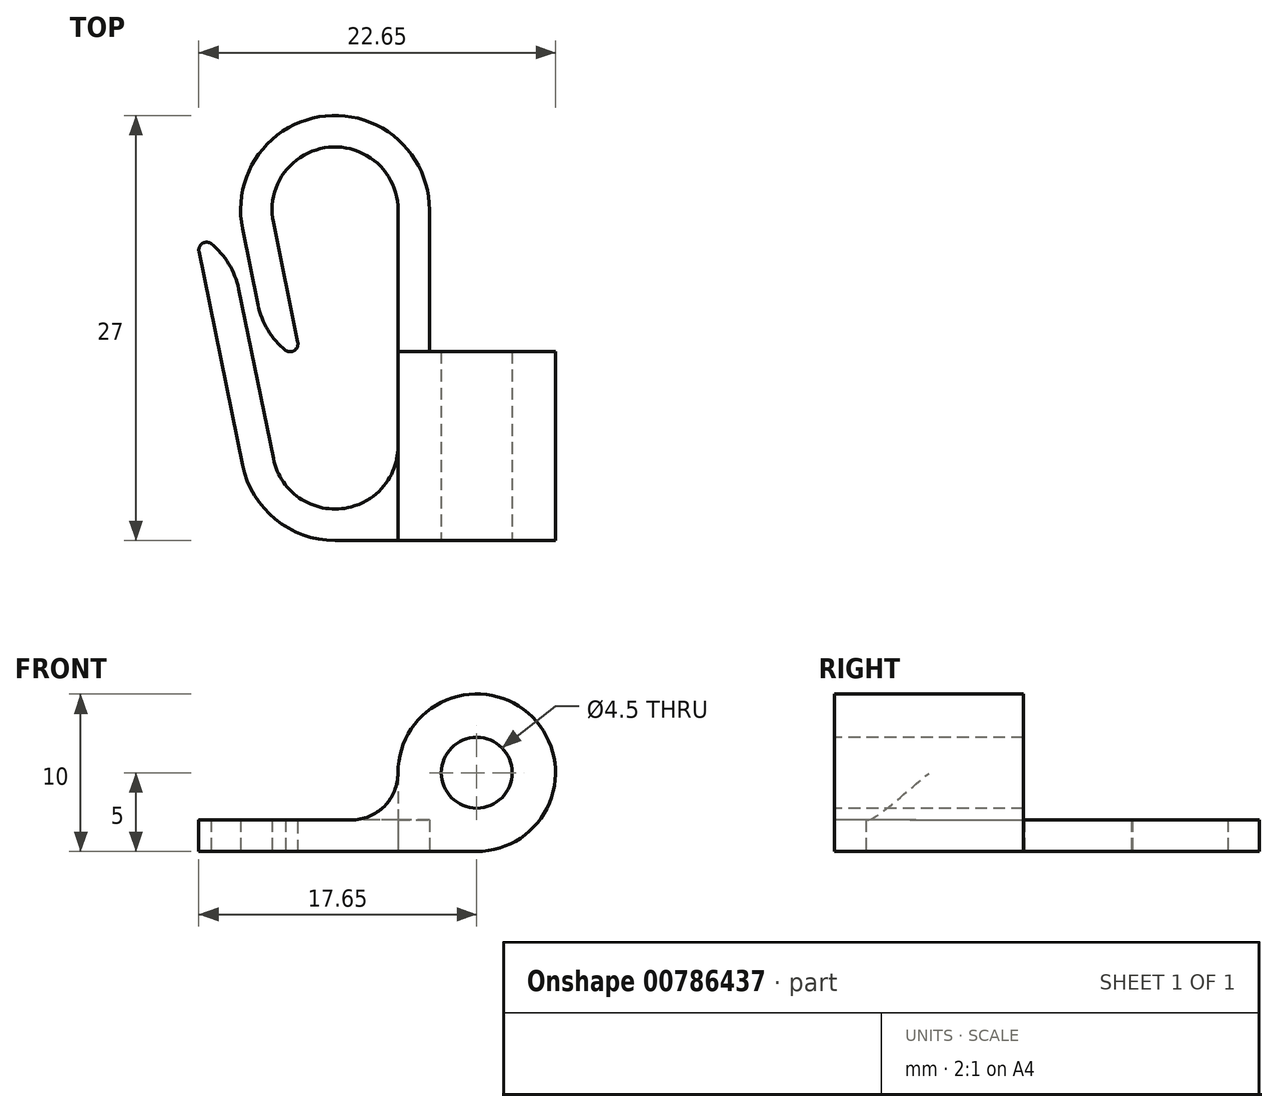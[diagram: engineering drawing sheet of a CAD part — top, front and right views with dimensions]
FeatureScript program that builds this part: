
annotation { "Feature Type Name" : "Feature", "Feature Type Description" : "" }
export const myFeature = defineFeature(function(context is Context, id is Id, definition is map)
    precondition{}
    {
        {
            var Q0;
            Q0=qCreatedBy(makeId("Top.planeOp"),FACE);
            var sketch = newSketch(context, id + "F0", { "sketchPlane" : qUnion([Q0])});
            skCircle(sketch, "E0", {"center": v(0, -5) * mm, "radius": 2.25 * mm});
            skCircle(sketch, "E1", {"center": v(0, -5) * mm, "radius": 5 * mm});
            skSolve(sketch);
        }
        {
            var Q0;
            Q0 = qSketchRegion(id + "F0", true);
            extrude(context, id + "F1", {"entities" : qUnion([Q0]), "endBound" : BoundingType.SYMMETRIC, "depth" : 12 * mm, "offsetDistance" : 25 * mm});
        }
        {
            var Q0;
            Q0=qCreatedBy(makeId("Front.planeOp"),FACE);
            var sketch = newSketch(context, id + "F2", { "sketchPlane" : qUnion([Q0])});
            skLineSegment(sketch, "E2", {"start": v(0, 23.91) * mm, "end": v(0, -9.96) * mm, "construction": true});
            skArc(sketch, "E3", {"start": v(-3, 15) * mm, "mid": v(-9.6, 20.97) * mm, "end": v(-14.88, 13.8) * mm});
            skArc(sketch, "E4", {"start": v(-5, 15) * mm, "mid": v(-9.4, 18.98) * mm, "end": v(-12.92, 14.2) * mm});
            skArc(sketch, "E5", {"start": v(-14.88, -1.2) * mm, "mid": v(-12.8, -4.65) * mm, "end": v(-9, -6) * mm});
            skArc(sketch, "E6", {"start": v(-12.92, -0.8) * mm, "mid": v(-8.6, -3.98) * mm, "end": v(-5, 0) * mm});
            skLineSegment(sketch, "E7", {"start": v(-3, 15) * mm, "end": v(-3, 6) * mm});
            skLineSegment(sketch, "E8", {"start": v(-5, 15) * mm, "end": v(-5, 0) * mm});
            skLineSegment(sketch, "E9", {"start": v(-14.88, -1.2) * mm, "end": v(-17.89, 13.53) * mm});
            skLineSegment(sketch, "E10", {"start": v(-12.92, -0.8) * mm, "end": v(-15.53, 11.97) * mm});
            skLineSegment(sketch, "E11", {"start": v(-14.88, 13.8) * mm, "end": v(-13.48, 6.97) * mm});
            skLineSegment(sketch, "E12", {"start": v(-12.92, 14.2) * mm, "end": v(-11.13, 5.41) * mm});
            skLineSegment(sketch, "E13", {"start": v(-13.48, 6.97) * mm, "end": v(-11.13, 5.41) * mm});
            skLineSegment(sketch, "E14", {"start": v(-17.89, 13.53) * mm, "end": v(-15.53, 11.97) * mm});
            skLineSegment(sketch, "E15", {"start": v(-9, -6) * mm, "end": v(0, -6) * mm});
            skLineSegment(sketch, "E16", {"start": v(-3, 6) * mm, "end": v(0, 6) * mm});
            skLineSegment(sketch, "E17", {"start": v(0, 6) * mm, "end": v(0, -6) * mm});
            skLineSegment(sketch, "E18", {"start": v(-17.15, 0) * mm, "end": v(8.35, 0) * mm, "construction": true});
            skSolve(sketch);
        }
        {
            var Q0;
            Q0 = qSketchRegion(id + "F2", true);
            extrude(context, id + "F3", {"entities" : qUnion([Q0]), "operationType" : NewBodyOperationType.ADD, "depth" : 2 * mm, "offsetDistance" : 25 * mm});
        }
        {
            var Q0;
            Q0=makeQuery(id+"F3.opExtrude","SWEPT_EDGE",EDGE,{"disambiguationData":[OSD([sQuery(id+"F2.wireOp",EDGE,"E12"),sQuery(id+"F2.wireOp",EDGE,"E13")])]});
            var Q1;
            Q1=makeQuery(id+"F3.opExtrude","SWEPT_EDGE",EDGE,{"disambiguationData":[OSD([sQuery(id+"F2.wireOp",EDGE,"E9"),sQuery(id+"F2.wireOp",EDGE,"E14")])]});
            fillet(context, id + "F4", {"entities" : qUnion([Q0, Q1]), "radius" : 0.5 * mm, "tangentPropagation" : true, "allowEdgeOverflow" : false});
        }
        {
            var Q0;
            Q0=makeQuery(id+"F3.opExtrude","SWEPT_EDGE",EDGE,{"disambiguationData":[OSD([sQuery(id+"F2.wireOp",EDGE,"E10"),sQuery(id+"F2.wireOp",EDGE,"E14")])]});
            var Q1;
            Q1=makeQuery(id+"F3.opExtrude","SWEPT_EDGE",EDGE,{"disambiguationData":[OSD([sQuery(id+"F2.wireOp",EDGE,"E11"),sQuery(id+"F2.wireOp",EDGE,"E13")])]});
            fillet(context, id + "F5", {"entities" : qUnion([Q0, Q1]), "radius" : 5 * mm, "tangentPropagation" : true, "allowEdgeOverflow" : false});
        }
        {
            var Q0;
            Q0=makeQuery(id+"F3.boolean.opBoolean","INTERSECT",EDGE,{"derivedFrom":[makeQuery(id+"F1.opExtrude","SWEPT_FACE",FACE,{"disambiguationData":[OSD([sQuery(id+"F0.wireOp",EDGE,"E1")])]}),makeQuery(id+"F3.opExtrude","CAP_FACE",FACE,{"disambiguationData":[OSD([sQuery(id+"F2.wireOp",EDGE,"E3"),sQuery(id+"F2.wireOp",EDGE,"E4"),sQuery(id+"F2.wireOp",EDGE,"E5"),sQuery(id+"F2.wireOp",EDGE,"E6"),sQuery(id+"F2.wireOp",EDGE,"E7"),sQuery(id+"F2.wireOp",EDGE,"E8"),sQuery(id+"F2.wireOp",EDGE,"E9"),sQuery(id+"F2.wireOp",EDGE,"E10"),sQuery(id+"F2.wireOp",EDGE,"E11"),sQuery(id+"F2.wireOp",EDGE,"E12"),sQuery(id+"F2.wireOp",EDGE,"E13"),sQuery(id+"F2.wireOp",EDGE,"E14"),sQuery(id+"F2.wireOp",EDGE,"E15"),sQuery(id+"F2.wireOp",EDGE,"E16"),sQuery(id+"F2.wireOp",EDGE,"E17")])],"isStart":false})]});
            fillet(context, id + "F6", {"entities" : qUnion([Q0]), "radius" : 2.98 * mm, "tangentPropagation" : true, "allowEdgeOverflow" : false});
        }
        {
            var Q0;
            Q0=makeQuery(id+"F1.opExtrude","SWEPT_BODY",BODY,{"disambiguationData":[OSD([sQuery(id+"F0.wireOp",EDGE,"E0"),sQuery(id+"F0.wireOp",EDGE,"E1")])]});
            var Q1;
            Q1=sQuery(id+"F2.wireOp",EDGE,"E18");
            transform(context, id + "F7", {"entities" : qUnion([Q0]), "transformType" : TransformType.ROTATION, "transformAxis" : qUnion([Q1]), "angle" : 90 * degree, "oppositeDirection" : true, "makeCopy" : false});
        }
    });
